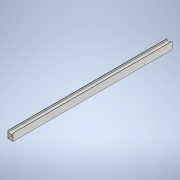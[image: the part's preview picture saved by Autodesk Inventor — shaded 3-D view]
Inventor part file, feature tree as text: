
AUTODESK INVENTOR PART (.ipt)
format: ipt  version: 2021 (Build 250183000, 183)  size: 116,736 bytes
history: native  units: in
note: dims shown in document units (in); Inventor stores cm internally (conversion verified against a paired STEP export)
features: extrude x1, sketch x1
ambient origin geometry x8: Origin, YZ Plane, XZ Plane, XY Plane, X Axis, Y Axis, Z Axis, Center Point
bodies: Solid1 (feature_tree)
feature tree (2):
  extrude  "Extrusion1"  Depth=7.75in
  sketch  "Sketch1"  dims[d6=3.0in d7=7.75in d8=0.5in d9=240.0in d10=0.0in d11=7.75in d12=0.5in d25=0.5in d26=0.0344in d27=0.5in d28=0.0344in]
